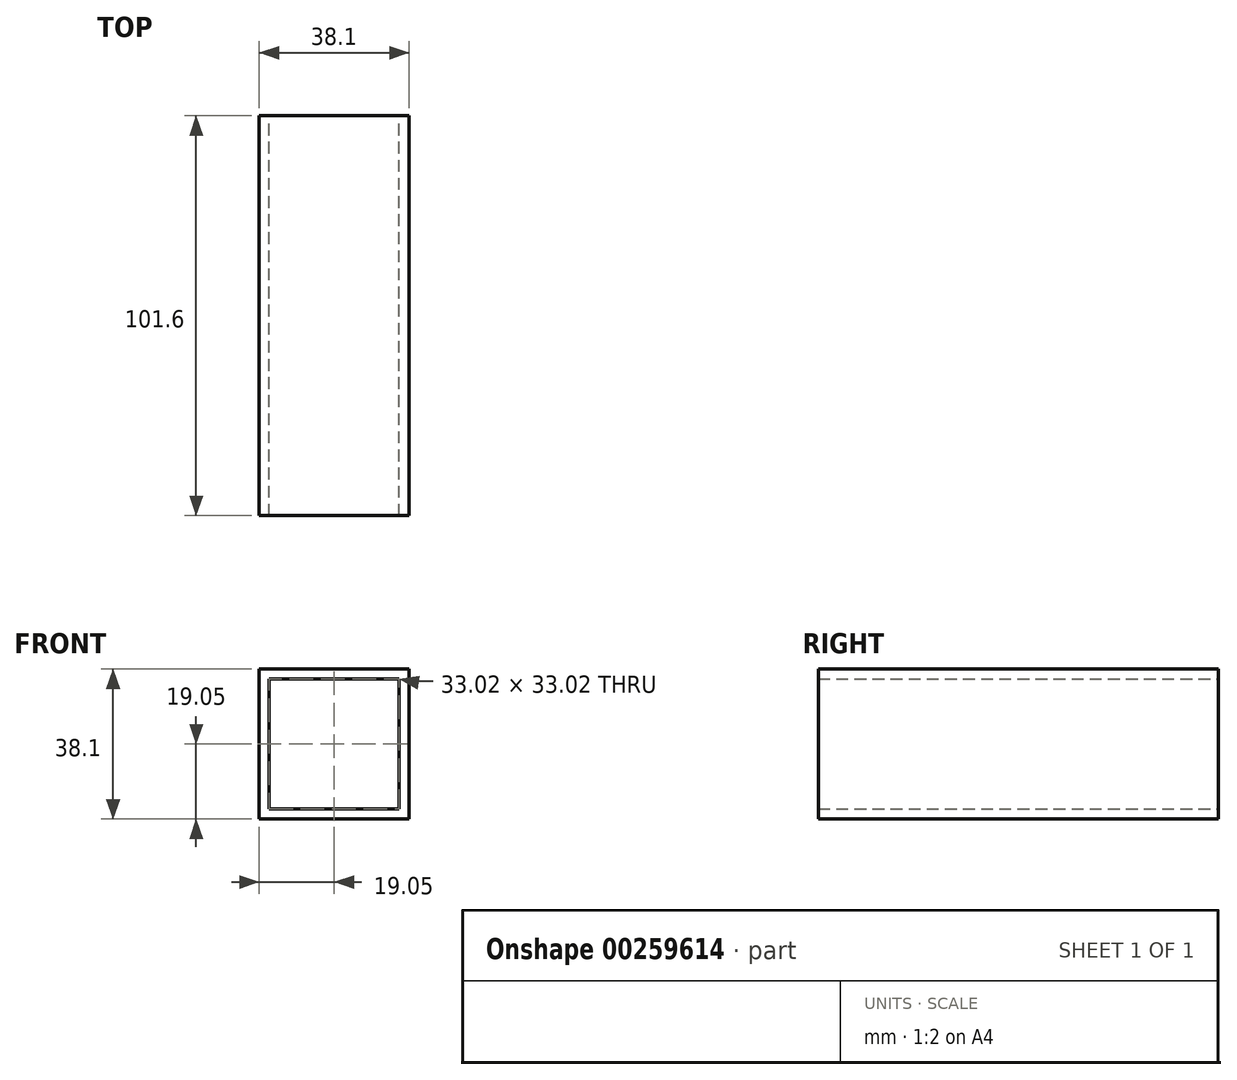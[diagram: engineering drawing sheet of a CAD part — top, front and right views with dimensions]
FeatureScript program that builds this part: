
annotation { "Feature Type Name" : "Feature", "Feature Type Description" : "" }
export const myFeature = defineFeature(function(context is Context, id is Id, definition is map)
    precondition{}
    {
        {
            var Q0;
            Q0=qCreatedBy(makeId("Front.planeOp"),FACE);
            var sketch = newSketch(context, id + "F0", { "sketchPlane" : qUnion([Q0])});
            skLineSegment(sketch, "E0.bottom", {"start": v(19.05, -19.05) * mm, "end": v(-19.05, -19.05) * mm});
            skLineSegment(sketch, "E0.top", {"start": v(19.05, 19.05) * mm, "end": v(-19.05, 19.05) * mm});
            skLineSegment(sketch, "E0.left", {"start": v(19.05, -19.05) * mm, "end": v(19.05, 19.05) * mm});
            skLineSegment(sketch, "E0.right", {"start": v(-19.05, -19.05) * mm, "end": v(-19.05, 19.05) * mm});
            skPoint(sketch, "E0.middle", {"position": v(0, 0) * mm});
            skLineSegment(sketch, "E1.bottom", {"start": v(16.51, -16.51) * mm, "end": v(-16.51, -16.51) * mm});
            skLineSegment(sketch, "E1.top", {"start": v(16.51, 16.51) * mm, "end": v(-16.51, 16.51) * mm});
            skLineSegment(sketch, "E1.left", {"start": v(16.51, -16.51) * mm, "end": v(16.51, 16.51) * mm});
            skLineSegment(sketch, "E1.right", {"start": v(-16.51, -16.51) * mm, "end": v(-16.51, 16.51) * mm});
            skSolve(sketch);
        }
        {
            var Q0;
            Q0=makeQuery(id+"F0.imprint","IMPRINT",FACE,{"disambiguationData":[TD([[makeQuery(id+"F0.imprint","IMPRINT",EDGE,{"derivedFrom":sQuery(id+"F0.wireOp",EDGE,"E0.bottom")}),-1.0]])]});
            extrude(context, id + "F1", {"entities" : qUnion([Q0]), "depth" : 101.6 * mm});
        }
        {
            var Q0;
            Q0=qCreatedBy(makeId("Right.planeOp"),FACE);
            var sketch = newSketch(context, id + "F2", { "sketchPlane" : qUnion([Q0])});
            skLineSegment(sketch, "E2.bottom", {"start": v(0, 16.51) * mm, "end": v(3.81, 16.51) * mm});
            skLineSegment(sketch, "E2.top", {"start": v(0, 29.21) * mm, "end": v(3.8, 29.21) * mm});
            skLineSegment(sketch, "E2.left", {"start": v(0, 16.51) * mm, "end": v(0, 29.21) * mm});
            skLineSegment(sketch, "E2.right", {"start": v(3.81, 16.51) * mm, "end": v(3.8, 29.21) * mm});
            skLineSegment(sketch, "E3.bottom", {"start": v(3.8, 29.21) * mm, "end": v(29.21, 29.21) * mm});
            skLineSegment(sketch, "E3.top", {"start": v(3.8, 25.4) * mm, "end": v(29.21, 25.4) * mm});
            skLineSegment(sketch, "E3.left", {"start": v(3.8, 29.21) * mm, "end": v(3.8, 25.4) * mm});
            skLineSegment(sketch, "E3.right", {"start": v(29.21, 29.21) * mm, "end": v(29.21, 25.4) * mm});
            skLineSegment(sketch, "E4.bottom", {"start": v(0, -16.51) * mm, "end": v(3.8, -16.51) * mm});
            skLineSegment(sketch, "E4.top", {"start": v(0, -29.21) * mm, "end": v(3.81, -29.21) * mm});
            skLineSegment(sketch, "E4.left", {"start": v(0, -16.51) * mm, "end": v(0, -29.21) * mm});
            skLineSegment(sketch, "E4.right", {"start": v(3.8, -16.51) * mm, "end": v(3.81, -29.21) * mm});
            skLineSegment(sketch, "E5.bottom", {"start": v(3.81, -29.21) * mm, "end": v(29.21, -29.21) * mm});
            skLineSegment(sketch, "E5.top", {"start": v(3.8, -25.4) * mm, "end": v(29.21, -25.4) * mm});
            skLineSegment(sketch, "E5.left", {"start": v(3.81, -29.21) * mm, "end": v(3.8, -25.4) * mm});
            skLineSegment(sketch, "E5.right", {"start": v(29.21, -29.21) * mm, "end": v(29.21, -25.4) * mm});
            skSolve(sketch);
        }
        {
            var Q0;
            Q0 = qSketchRegion(id + "F2", true);
            extrude(context, id + "F3", {"entities" : qUnion([Q0]), "depth" : 38.1 * mm, "symmetric" : true});
        }
        {
            var Q0;
            Q0=makeQuery(id+"F3.opExtrude","SWEPT_FACE",FACE,{"disambiguationData":[OSD([sQuery(id+"F2.wireOp",EDGE,"E2.top"),sQuery(id+"F2.wireOp",EDGE,"E3.bottom")])]});
            var sketch = newSketch(context, id + "F4", { "sketchPlane" : qUnion([Q0])});
            skCircle(sketch, "E6", {"center": v(0, 16.5) * mm, "radius": 6.35 * mm});
            skSolve(sketch);
        }
        {
            var Q0;
            Q0=makeQuery(id+"F4.imprint","IMPRINT",FACE,{"disambiguationData":[TD([[makeQuery(id+"F4.imprint","IMPRINT",EDGE,{"derivedFrom":sQuery(id+"F4.wireOp",EDGE,"E6")}),1.0]])]});
            extrude(context, id + "F5", {"entities" : qUnion([Q0]), "operationType" : NewBodyOperationType.REMOVE, "endBound" : BoundingType.THROUGH_ALL, "oppositeDirection" : true, "depth" : 152.4 * mm});
        }
        {
            var Q0;
            Q0=makeQuery(id+"F3.opExtrude","SWEPT_FACE",FACE,{"disambiguationData":[OSD([sQuery(id+"F2.wireOp",EDGE,"E4.top"),sQuery(id+"F2.wireOp",EDGE,"E5.bottom")])]});
            var sketch = newSketch(context, id + "F6", { "sketchPlane" : qUnion([Q0])});
            skCircle(sketch, "E7", {"center": v(0, -16.51) * mm, "radius": 6.35 * mm});
            skSolve(sketch);
        }
        {
            var Q0;
            Q0=makeQuery(id+"F6.imprint","IMPRINT",FACE,{"disambiguationData":[TD([[makeQuery(id+"F6.imprint","IMPRINT",EDGE,{"derivedFrom":sQuery(id+"F6.wireOp",EDGE,"E7")}),1.0]])]});
            extrude(context, id + "F7", {"entities" : qUnion([Q0]), "operationType" : NewBodyOperationType.REMOVE, "endBound" : BoundingType.THROUGH_ALL, "oppositeDirection" : true, "depth" : 25.4 * mm});
        }
    });
